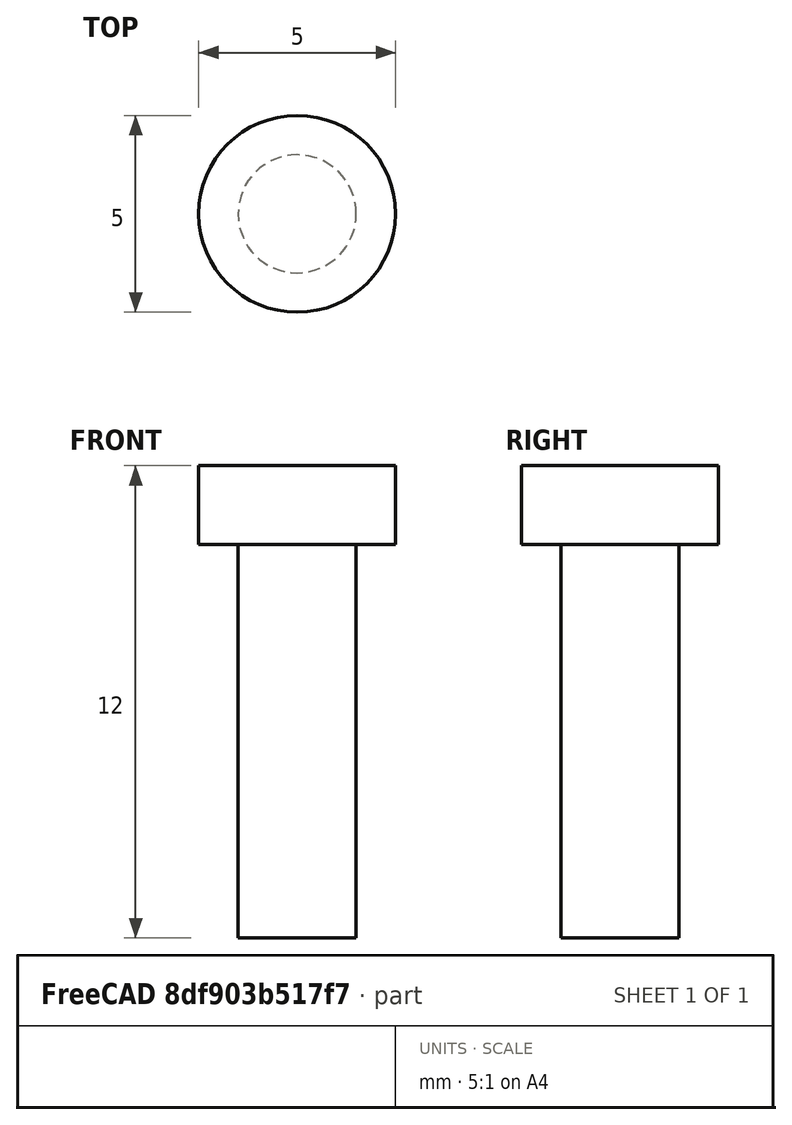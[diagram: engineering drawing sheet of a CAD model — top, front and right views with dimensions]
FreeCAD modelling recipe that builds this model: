
FCSTD DOCUMENT  (FreeCAD 0.18R14555 (Git shallow))
Label: m3-10
License: All rights reserved
LicenseURL: http://en.wikipedia.org/wiki/All_rights_reserved
objects: Sketcher::SketchObject×1, PartDesign::Revolution×1, PartDesign::Body×1
note: 4 computed .brp shape members not serialized (recipe doc carries the construction recipe); baked Part::Feature solids carry a one-line shape summary decoded from their .brp

FEATURE [Sketcher::SketchObject] Sketch
  MapMode = 5
  Placement = pos=(0,0,0) rot=(1,0,0;1.5708rad)
  Support = -> [XZ_Plane]
  sketch-geometry (6):
    g0: LineSegment StartX=0 StartY=0 StartZ=0 EndX=0 EndY=12 EndZ=0
    g1: LineSegment StartX=0 StartY=12 StartZ=0 EndX=2.5 EndY=12 EndZ=0
    g2: LineSegment StartX=2.5 StartY=12 StartZ=0 EndX=2.5 EndY=10 EndZ=0
    g3: LineSegment StartX=2.5 StartY=10 StartZ=0 EndX=1.5 EndY=10 EndZ=0
    g4: LineSegment StartX=1.5 StartY=10 StartZ=0 EndX=1.5 EndY=0 EndZ=0
    g5: LineSegment StartX=1.5 StartY=0 StartZ=0 EndX=0 EndY=0 EndZ=0
  constraints (17):
    c: Vertical(g0)
    c: Coincident(g0,g1)
    c: Horizontal(g1)
    c: Coincident(g1,g2)
    c: Coincident(g2,g3)
    c: Horizontal(g3)
    c: Coincident(g3,g4)
    c: Vertical(g4)
    c: Coincident(g4,g5)
    c: Horizontal(g5)
    c: Coincident(g0,g-1)
    c: Coincident(g5,g0)
    c: DistanceX(g5,g5) = 1.5
    c: DistanceY(g4,g4) = 10
    c: Vertical(g2)
    c: DistanceX(g1,g1) = 2.5
    c: DistanceY(g2,g2) = 2
FEATURE [PartDesign::Revolution] Revolution
  Angle = 360
  Axis = (0,2e-16,1)
  Base = (0,0,0)
  Placement = pos=(0,0,0) rot=(1,0,0;1.5708rad)
  Profile = -> Sketch
  ReferenceAxis = -> Sketch [V_Axis]
  Reversed = true
FEATURE [PartDesign::Body] Body
  Group = -> [Sketch,Revolution]
  Origin = -> Origin
  Tip = -> Revolution
